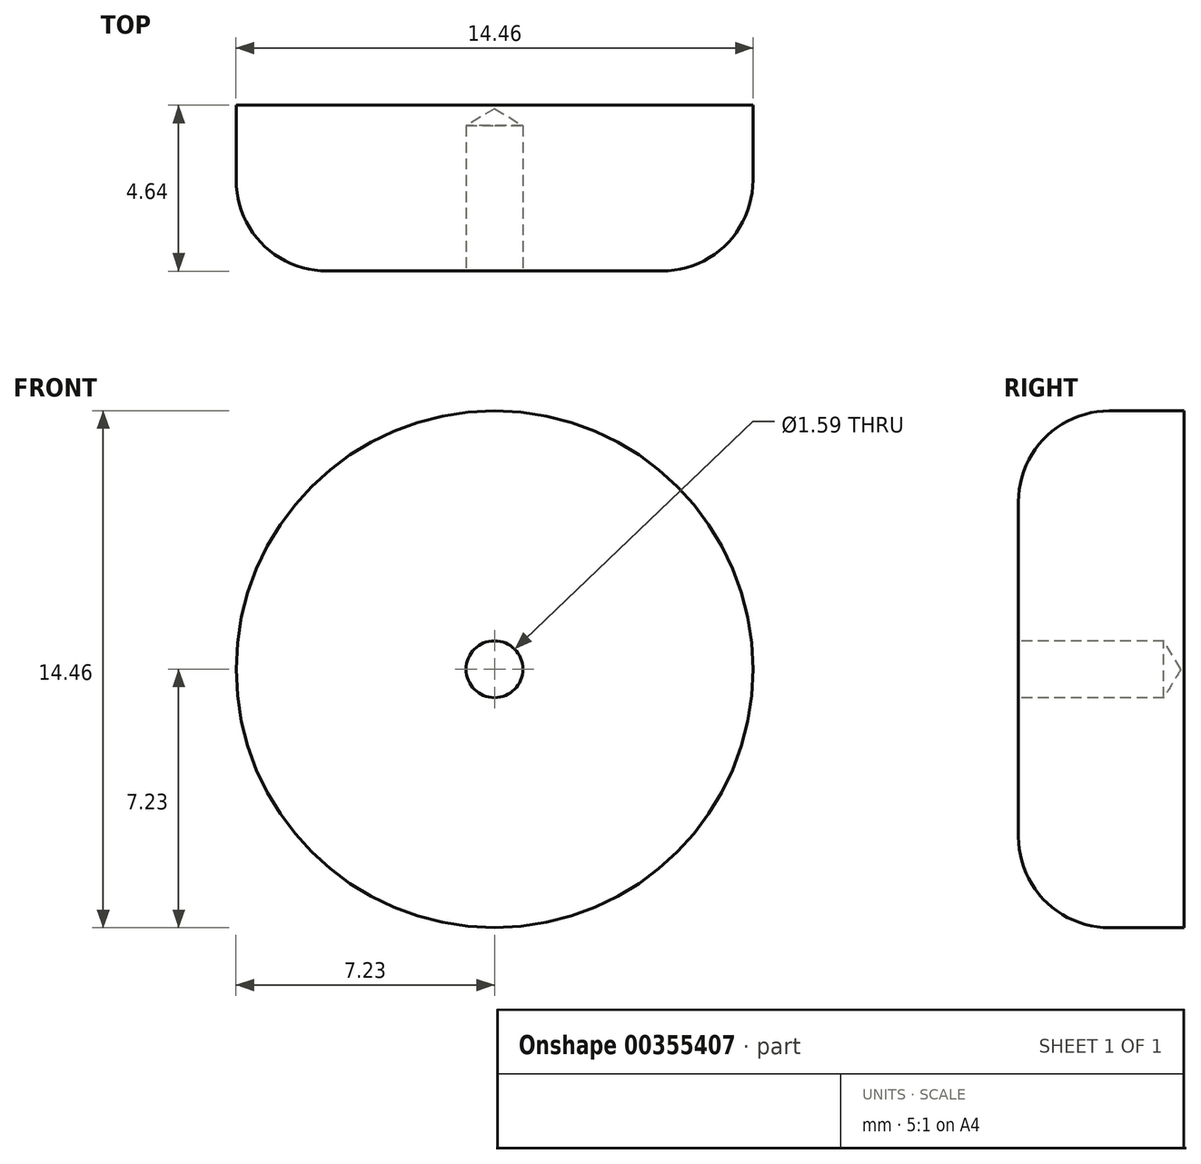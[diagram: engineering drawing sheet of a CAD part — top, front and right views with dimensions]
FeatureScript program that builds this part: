
annotation { "Feature Type Name" : "Feature", "Feature Type Description" : "" }
export const myFeature = defineFeature(function(context is Context, id is Id, definition is map)
    precondition{}
    {
        {
            var Q0;
            Q0=qCreatedBy(makeId("Front.planeOp"),FACE);
            var sketch = newSketch(context, id + "F0", { "sketchPlane" : qUnion([Q0])});
            skCircle(sketch, "E0", {"center": v(0, 0) * mm, "radius": 7.23 * mm});
            skSolve(sketch);
        }
        {
            var Q0;
            Q0 = qSketchRegion(id + "F0", true);
            extrude(context, id + "F1", {"entities" : qUnion([Q0]), "depth" : 4.64 * mm});
        }
        {
            var Q0;
            Q0=makeQuery(id+"F1.opExtrude","CAP_FACE",FACE,{"disambiguationData":[OSD([sQuery(id+"F0.wireOp",EDGE,"E0")])],"isStart":false});
            var sketch = newSketch(context, id + "F2", { "sketchPlane" : qUnion([Q0])});
            skPoint(sketch, "E1", {"position": v(0, 0) * mm});
            skSolve(sketch);
        }
        {
            var Q0;
            Q0=sQuery(id+"F2.wireOp",VERTEX,"E1");
            var Q1;
            Q1=makeQuery(id+"F1.opExtrude","SWEPT_BODY",BODY,{"disambiguationData":[OSD([sQuery(id+"F0.wireOp",EDGE,"E0")])]});
            hole(context, id + "F3", {"style" : HoleStyle.SIMPLE, "endStyle" : HoleEndStyle.BLIND, "holeDiameter" : 1.59 * mm, "holeDepth" : 4.06 * mm, "isTappedThrough" : true, "tappedDepth" : 12.7 * mm, "tapClearance" : 3, "startFromSketch" : true, "locations" : qUnion([Q0]), "scope" : qUnion([Q1])});
        }
        {
            var Q0;
            Q0=makeQuery(id+"F1.opExtrude","CAP_EDGE",EDGE,{"disambiguationData":[OSD([sQuery(id+"F0.wireOp",EDGE,"E0")])],"isStart":false});
            fillet(context, id + "F4", {"entities" : qUnion([Q0]), "radius" : 2.54 * mm, "tangentPropagation" : true, "allowEdgeOverflow" : false});
        }
    });
